# Revit family: Reece_Basin_LAUFEN_INO_Wall Basin_560 mm
name_source: partatom
category: Plumbing Fixtures
revit_build: Autodesk Revit 2018 (Build: 20190510_1515(x64)
units: mm (PartAtom-declared; Revit-internal decimal feet)

## family parameters
Always vertical = Yes
Cut with Voids When Loaded = Yes
Part Type = Normal
Room Calculation Point = Yes
Round Connector Dimension = Use Diameter
Shared = Yes
Work Plane-Based = Yes

## types (1)
- 1 Taphole_SaphirKeramik_White
    Default Elevation = 0 mm  [stored 0 ft]
    Description = LAUFEN Ino Wall Basin with Fixing Bolts with Overflow 1 Taphole 560mm White
    Disclaimer = THIS FILE IS THE PROPERTY OF THE REECE GROUP. IT MAY NOT BE REPRODUCED, REVERSE-ENGINEERED OR MODIFIED. ANY REPUBLICATION, TRANSMISSION OR DISTRIBUTION FOR THE PURPOSE OF COMMERCIALLY EXPLOITING THE FILES IS PROHIBITED.
    Keynote = Product #9507785, Reece_Basin_LAUFEN_INO_Wall Basin_560 mm - 1 Taphole_SaphirKeramik_White
    Manufacturer = LAUFEN
    Model = INO
    Reece_Basin_Outlet = 40 mm  [stored 0.131234 ft]
    Reece_Basin_Taphole 1 = Yes
    Reece_Detail_Additional = Integrated Overflow
    Reece_Detail_Connector = 1 Taphole
    Reece_Detail_Disclaimer = THIS FILE IS THE PROPERTY OF THE REECE GROUP. IT MAY NOT BE REPRODUCED, REVERSE-ENGINEERED OR MODIFIED. ANY REPUBLICATION, TRANSMISSION OR DISTRIBUTION FOR THE PURPOSE OF COMMERCIALLY EXPLOITING THE FILES IS PROHIBITED.
    Reece_Detail_Installation = Wall Basin
    Reece_Height_From_Level = 900 mm  [stored 2.95276 ft]
    Reece_Material_Main = Reece_SaphirKeramik_White
    Reece_Overall_Capacity = 5.9 L
    Reece_Overall_Height = 120 mm  [stored 0.393701 ft]
    Reece_Overall_Length = 450 mm  [stored 1.47638 ft]
    Reece_Overall_Width = 560 mm  [stored 1.83727 ft]
    Reece_Product_Brand = LAUFEN
    Reece_Product_Description = LAUFEN Ino Wall Basin with Fixing Bolts with Overflow 1 Taphole 560mm White
    Reece_Product_Mount = Wall Mounted
    Reece_Product_Number = 9507785
    Reece_Product_Sub Brand = INO
    Reece_Product_Type = Basin
    Reece_Product_Web Page = https://www.reece.com.au
    Type Comments = Basin
    URL = https://www.reece.com.au

note: [stored X ft] marks values corroborated as IEEE doubles in the binary element streams (Revit-internal decimal feet)

## geometry (parser evidence)
native form markers: Sweep x3
no freeform markers — native parametric forms only
